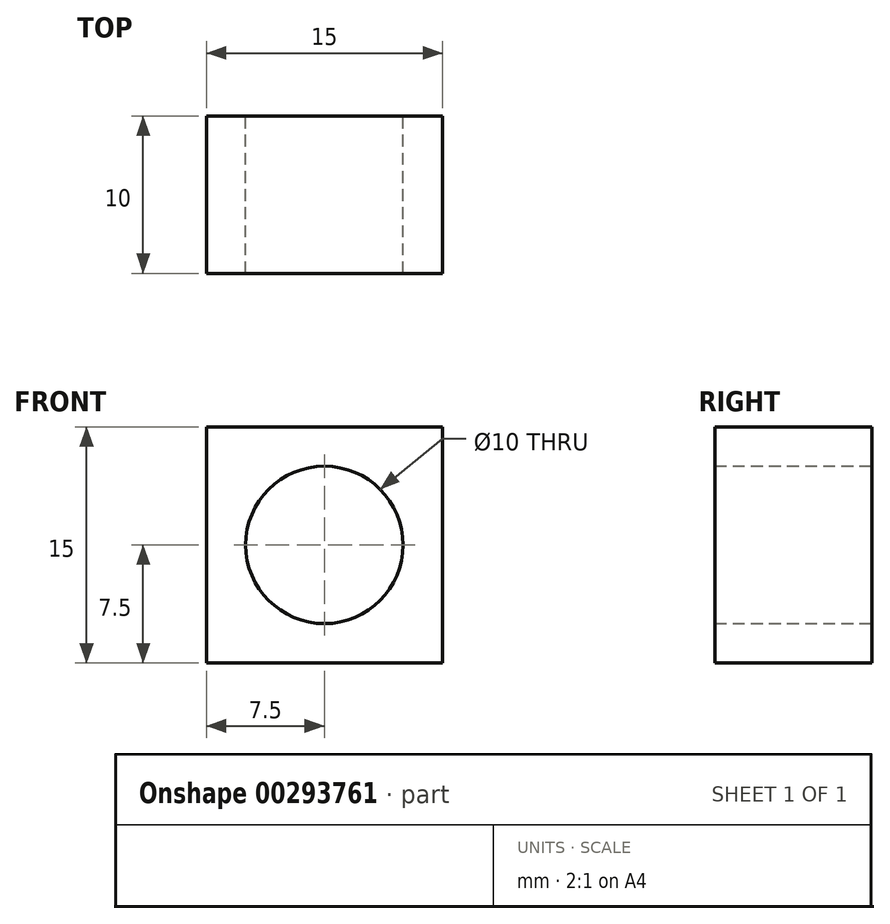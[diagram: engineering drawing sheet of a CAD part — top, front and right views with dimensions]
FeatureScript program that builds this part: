
annotation { "Feature Type Name" : "Feature", "Feature Type Description" : "" }
export const myFeature = defineFeature(function(context is Context, id is Id, definition is map)
    precondition{}
    {
        {
            var Q0;
            Q0=qCreatedBy(makeId("Front.planeOp"),FACE);
            var sketch = newSketch(context, id + "F0", { "sketchPlane" : qUnion([Q0])});
            skLineSegment(sketch, "E0.bottom", {"start": v(7.5, 7.5) * mm, "end": v(-7.5, 7.5) * mm});
            skLineSegment(sketch, "E0.top", {"start": v(7.5, -7.5) * mm, "end": v(-7.5, -7.5) * mm});
            skLineSegment(sketch, "E0.left", {"start": v(7.5, 7.5) * mm, "end": v(7.5, -7.5) * mm});
            skLineSegment(sketch, "E0.right", {"start": v(-7.5, 7.5) * mm, "end": v(-7.5, -7.5) * mm});
            skPoint(sketch, "E0.middle", {"position": v(0, 0) * mm});
            skCircle(sketch, "E1", {"center": v(0, 0) * mm, "radius": 5 * mm});
            skSolve(sketch);
        }
        {
            var Q0;
            Q0=makeQuery(id+"F0.imprint","IMPRINT",FACE,{"disambiguationData":[TD([[makeQuery(id+"F0.imprint","IMPRINT",EDGE,{"derivedFrom":sQuery(id+"F0.wireOp",EDGE,"E0.bottom")}),1.0]])]});
            extrude(context, id + "F1", {"entities" : qUnion([Q0]), "depth" : 10 * mm});
        }
    });
